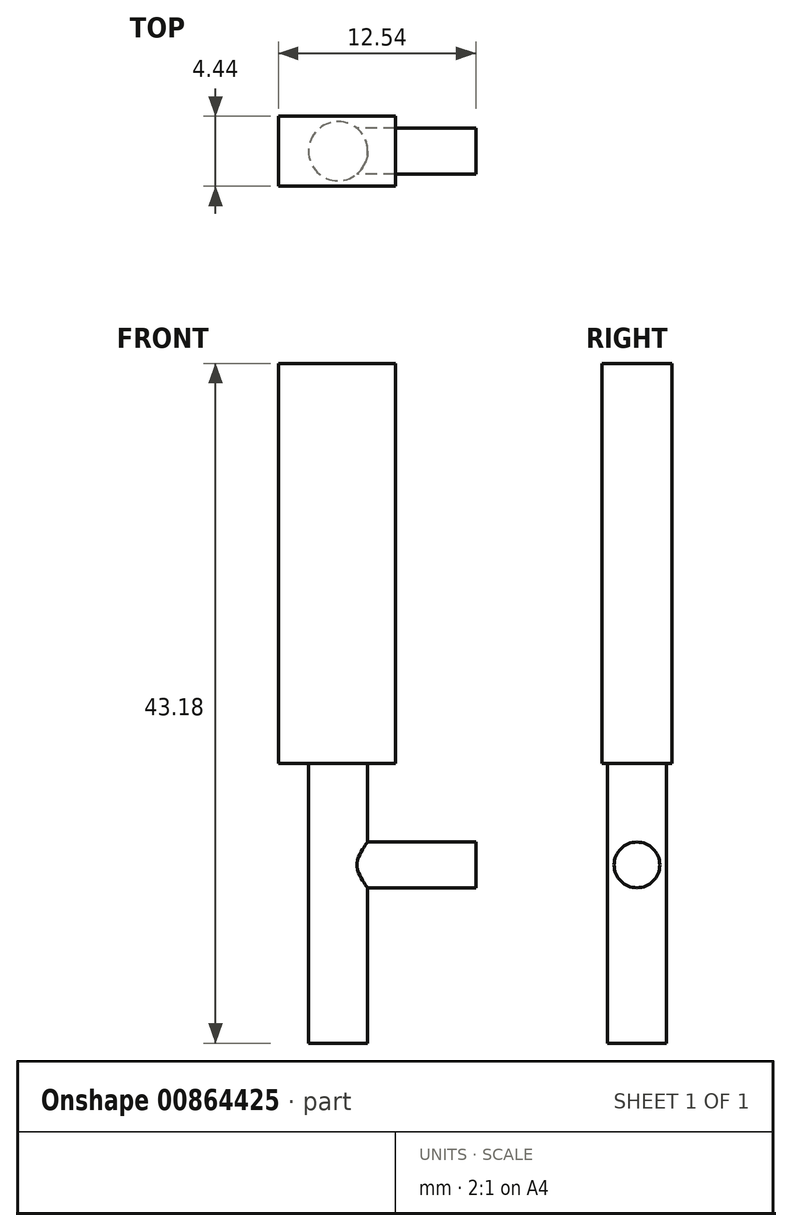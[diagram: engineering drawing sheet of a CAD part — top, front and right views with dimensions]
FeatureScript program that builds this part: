
annotation { "Feature Type Name" : "Feature", "Feature Type Description" : "" }
export const myFeature = defineFeature(function(context is Context, id is Id, definition is map)
    precondition{}
    {
        {
            var Q0;
            Q0=qCreatedBy(makeId("Right.planeOp"),FACE);
            var sketch = newSketch(context, id + "F0", { "sketchPlane" : qUnion([Q0])});
            skCircle(sketch, "E0", {"center": v(0, 11.32) * mm, "radius": 1.45 * mm});
            skSolve(sketch);
        }
        {
            var Q0;
            Q0=makeQuery(id+"F0.imprint","IMPRINT",FACE,{"disambiguationData":[TD([[makeQuery(id+"F0.imprint","IMPRINT",EDGE,{"derivedFrom":sQuery(id+"F0.wireOp",EDGE,"E0")}),1.0]])]});
            extrude(context, id + "F1", {"entities" : qUnion([Q0]), "depth" : 7.62 * mm, "offsetDistance" : 25.4 * mm});
        }
        {
            var Q0;
            Q0=qCreatedBy(makeId("Top.planeOp"),FACE);
            var sketch = newSketch(context, id + "F2", { "sketchPlane" : qUnion([Q0])});
            skCircle(sketch, "E1", {"center": v(-1.13, 0) * mm, "radius": 1.88 * mm});
            skSolve(sketch);
        }
        {
            var Q0;
            Q0=makeQuery(id+"F2.imprint","IMPRINT",FACE,{"disambiguationData":[TD([[makeQuery(id+"F2.imprint","IMPRINT",EDGE,{"derivedFrom":sQuery(id+"F2.wireOp",EDGE,"E1")}),1.0]])]});
            extrude(context, id + "F3", {"entities" : qUnion([Q0]), "operationType" : NewBodyOperationType.ADD, "depth" : 25.4 * mm, "offsetDistance" : 25.4 * mm});
        }
        {
            var Q0;
            Q0=qCreatedBy(makeId("Top.planeOp"),FACE);
            cPlane(context, id + "F4", {"entities" : qUnion([Q0]), "cplaneType" : CPlaneType.OFFSET, "offset" : 17.78 * mm, "width" : 152.4 * mm, "height" : 152.4 * mm});
        }
        {
            var Q0;
            Q0=qCreatedBy(id+"F4.planeOp",FACE);
            var sketch = newSketch(context, id + "F5", { "sketchPlane" : qUnion([Q0])});
            skLineSegment(sketch, "E2.bottom", {"start": v(-4.92, 2.2) * mm, "end": v(2.5, 2.2) * mm});
            skLineSegment(sketch, "E2.top", {"start": v(-4.92, -2.23) * mm, "end": v(2.5, -2.23) * mm});
            skLineSegment(sketch, "E2.left", {"start": v(-4.92, 2.2) * mm, "end": v(-4.92, -2.23) * mm});
            skLineSegment(sketch, "E2.right", {"start": v(2.5, 2.2) * mm, "end": v(2.5, -2.23) * mm});
            skSolve(sketch);
        }
        {
            var Q0;
            Q0=makeQuery(id+"F5.imprint","IMPRINT",FACE,{"disambiguationData":[TD([[makeQuery(id+"F5.imprint","IMPRINT",EDGE,{"derivedFrom":sQuery(id+"F5.wireOp",EDGE,"E2.bottom")}),-1.0]])]});
            extrude(context, id + "F6", {"entities" : qUnion([Q0]), "operationType" : NewBodyOperationType.ADD, "depth" : 25.4 * mm, "offsetDistance" : 25.4 * mm});
        }
    });
